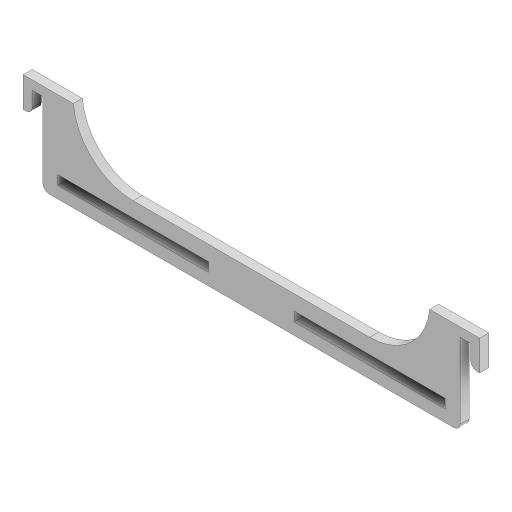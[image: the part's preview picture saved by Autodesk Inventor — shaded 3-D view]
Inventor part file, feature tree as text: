
AUTODESK INVENTOR PART (.ipt)
format: ipt  version: 2023 (Build 270158000, 158)  size: 153,088 bytes
history: native  units: mm
features: extrude x2, sketch x2
ambient origin geometry x8: Origin, YZ Plane, XZ Plane, XY Plane, X Axis, Y Axis, Z Axis, Center Point
bodies: Solid1 (feature_tree)
feature tree (4):
  extrude  "Extrusion1"  Depth=30.0mm
  extrude  "Extrusion2"  Depth=3.0mm
  sketch  "Sketch1"  dims[d0=138.5mm d1=30.0mm]
  sketch  "Sketch2"  dims[d2=3.5mm d3=3.0mm d4=3.0mm d5=10.0mm d6=3.5mm d7=3.0mm d8=3.0mm d9=10.0mm d10=2.0mm d11=3.0mm d12=20.0mm d13=5.0mm d14=50.0mm d15=3.0mm d16=5.0mm d17=50.0mm d18=2.0mm d19=3.0mm d20=0.0mm d21=5.0mm d22=10.0mm d23=10.0mm d24=20.0mm d25=10.0mm d26=0.0mm]
